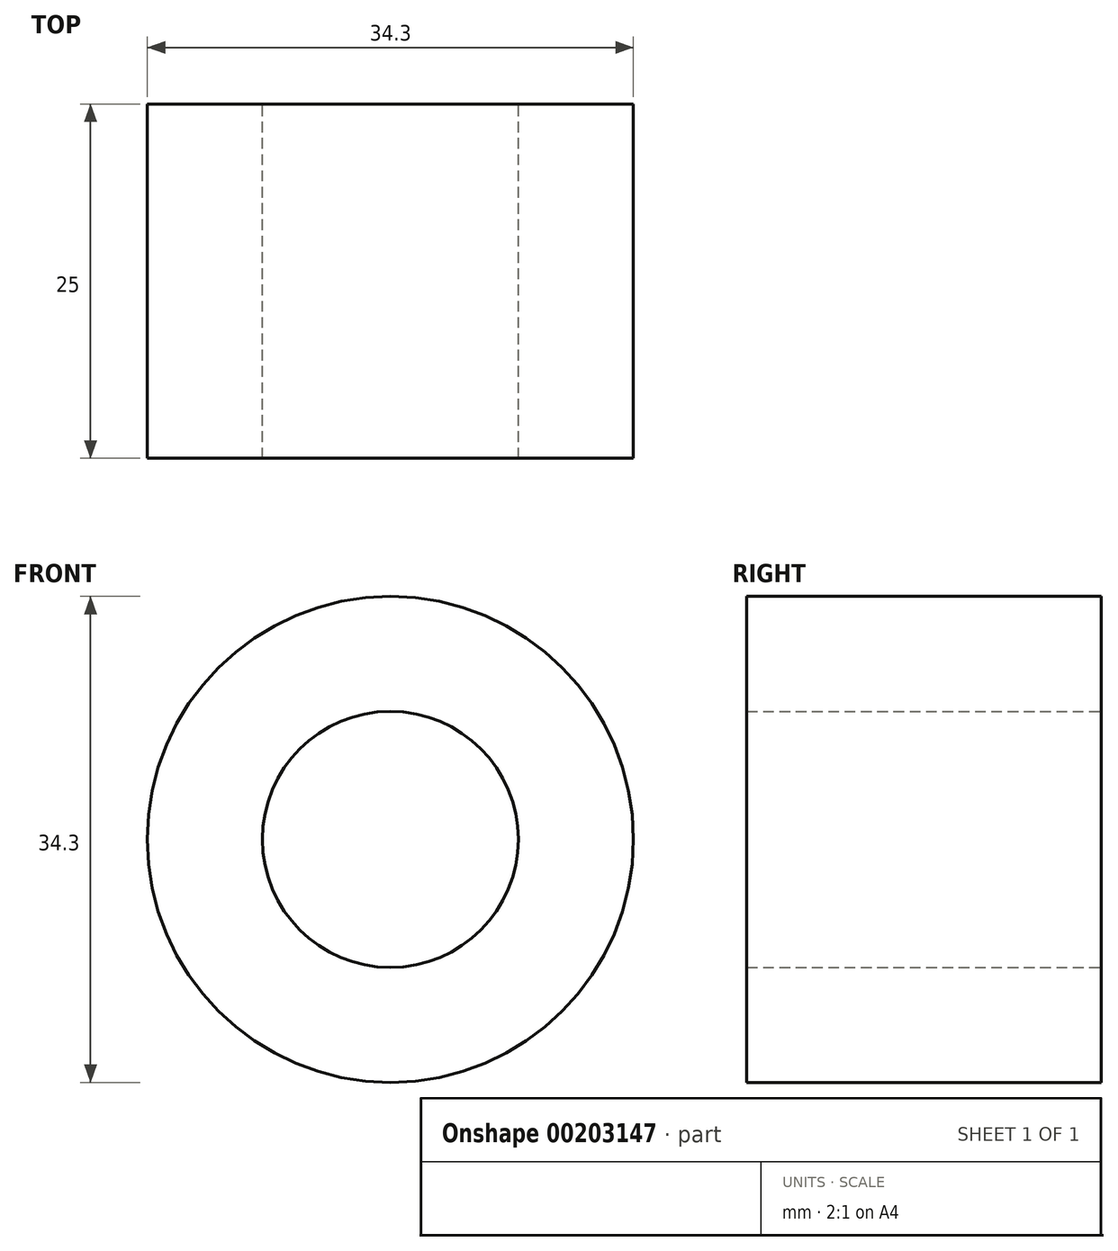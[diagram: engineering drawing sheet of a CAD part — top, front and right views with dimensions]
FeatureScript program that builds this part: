
annotation { "Feature Type Name" : "Feature", "Feature Type Description" : "" }
export const myFeature = defineFeature(function(context is Context, id is Id, definition is map)
    precondition{}
    {
        {
            var Q0;
            Q0=qCreatedBy(makeId("Front.planeOp"),FACE);
            var sketch = newSketch(context, id + "F0", { "sketchPlane" : qUnion([Q0])});
            skCircle(sketch, "E0", {"center": v(-36.73, 37.43) * mm, "radius": 17.15 * mm});
            skCircle(sketch, "E1", {"center": v(-36.73, 37.43) * mm, "radius": 9.03 * mm});
            skSolve(sketch);
        }
        {
            var Q0;
            Q0=makeQuery(id+"F0.imprint","IMPRINT",FACE,{"disambiguationData":[TD([[makeQuery(id+"F0.imprint","IMPRINT",EDGE,{"derivedFrom":sQuery(id+"F0.wireOp",EDGE,"E0")}),1.0]])]});
            extrude(context, id + "F1", {"entities" : qUnion([Q0]), "depth" : 25 * mm});
        }
    });
